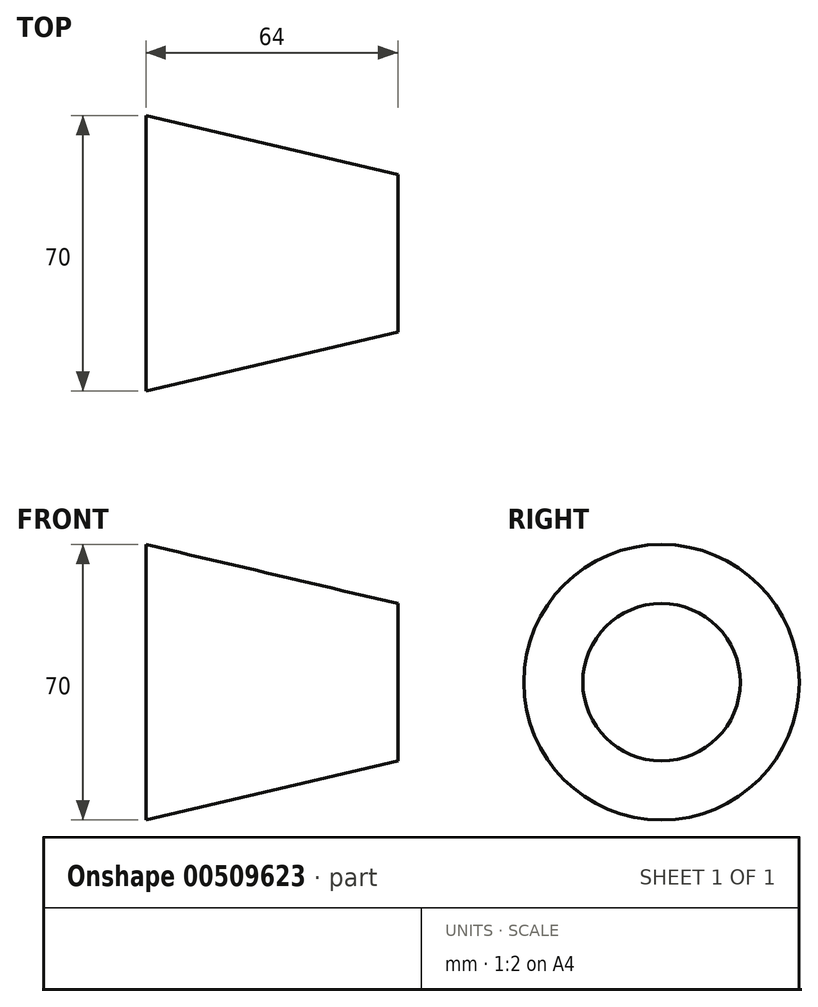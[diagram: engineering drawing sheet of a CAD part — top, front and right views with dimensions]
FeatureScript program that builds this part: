
annotation { "Feature Type Name" : "Feature", "Feature Type Description" : "" }
export const myFeature = defineFeature(function(context is Context, id is Id, definition is map)
    precondition{}
    {
        {
            var Q0;
            Q0=qCreatedBy(makeId("Front.planeOp"),FACE);
            var sketch = newSketch(context, id + "F0", { "sketchPlane" : qUnion([Q0])});
            skLineSegment(sketch, "E0", {"start": v(-46.43, 0) * mm, "end": v(17.57, 0) * mm});
            skLineSegment(sketch, "E1", {"start": v(-46.43, 0) * mm, "end": v(-46.43, 35) * mm});
            skLineSegment(sketch, "E2", {"start": v(-46.43, 35) * mm, "end": v(17.57, 20) * mm});
            skLineSegment(sketch, "E3", {"start": v(17.57, 0) * mm, "end": v(17.57, 20) * mm});
            skSolve(sketch);
        }
        {
            var Q0;
            Q0=makeQuery(id+"F0.imprint","IMPRINT",FACE,{"disambiguationData":[TD([[makeQuery(id+"F0.imprint","IMPRINT",EDGE,{"derivedFrom":sQuery(id+"F0.wireOp",EDGE,"E0")}),1.0]])]});
            var Q1;
            Q1=sQuery(id+"F0.wireOp",EDGE,"E2");
            var Q2;
            Q2=sQuery(id+"F0.wireOp",EDGE,"E0");
            revolve(context, id + "F1", {"entities" : qUnion([Q0]), "surfaceEntities" : qUnion([Q1]), "axis" : qUnion([Q2]), "revolveType" : RevolveType.FULL});
        }
    });
